# Revit family: Artek_Chairs_Aslak Chair_Aslak Chair
name_source: partatom
category: Furniture
revit_build: Autodesk Revit 2018 (Build: 20170223_1515(x64)
units: mm (PartAtom-declared; Revit-internal decimal feet)

## family parameters
Always vertical = Yes
Cut with Voids When Loaded = No
OmniClass Number = 23.40.20.14.14.11
OmniClass Title = Chairs
Room Calculation Point = No
Shared = No
Work Plane-Based = No

## types (5) — shared parameters
AssetType = Movable
BIMObjectName = Artek_Chairs_Aslak Chair_Aslak Chair
Brand = Artek
Category = Chairs
ConvergoRefNr = 0190-2009-0027-FI
Description = The beechwood Aslak Chair is as elegant as it is versatile. Stackable, lightweight, and eminently inviting, it fits equally well in restaurants, meeting rooms, or homes.
Designer = Ilmari Tapiovaara
DurationUnit = Years
IfcExportAs = IfcFurnishingElementType
IfcExportType = CHAIR
Manufacturer = Artek
ManufacturerName = Artek
ManufacturerURL = https://www.artek.fi
Material = Wood
NBSDescription = Domestic chairs
NBSReference = 45-35-20/365
Name = Aslak Chair
NominalDepth = 506 mm
NominalHeight = 761 mm
NominalLength = 531 mm
ProductInformation = The beechwood Aslak Chair is as elegant as it is versatile. Stackable, lightweight, and eminently inviting, it fits equally well in restaurants, meeting rooms, or homes.
Shape = Sculptured
Size = 530x760x500 mm
URL = https://www.artek.fi
Uniclass2 = Pr_40_50_12_48
Uniclass2015Description = Dining chairs
Uniclass2015Reference = Pr_40_50_12_22
Version = 1
VersionDate = 11/3/2020
WarrantyDurationUnit = Years
zero-valued in all types: Cost

## per-type parameters (varying)
| type | ChairMaterial | Color | HighestSeatingHeight | LowestSeatingHeight | MainColor | ModelNumber | SeatingHeight |
| Aslak Chair, 28104401 | Black laquered | Black | 459 mm | 459 mm | Black | 28104401 | 459 mm |
| Aslak Chair, 28104402 | White laquered | White | 459 mm | 459 mm | White | 28104402 | 459 mm |
| Aslak Chair, 28104403 | Grey laquered | Grey | 459 mm | 459 mm | Grey | 28104403 | 459 mm |
| Aslak Chair, 28104404 | Petrol laquered | Petrol | 460 mm  [stored 1.50919 ft] | 460 mm  [stored 1.50919 ft] | Petrol | 28104404 | 460 mm  [stored 1.50919 ft] |
| Aslak Chair, 28104405 | Red laquered | Red | 459 mm | 459 mm | Red | 28104405 | 459 mm |

note: column(s) folded — value = type name in every type: Model

note: [stored X ft] marks values corroborated as IEEE doubles in the binary element streams (Revit-internal decimal feet)

## geometry (parser evidence)
native form markers: Sweep x4
no freeform markers — native parametric forms only
